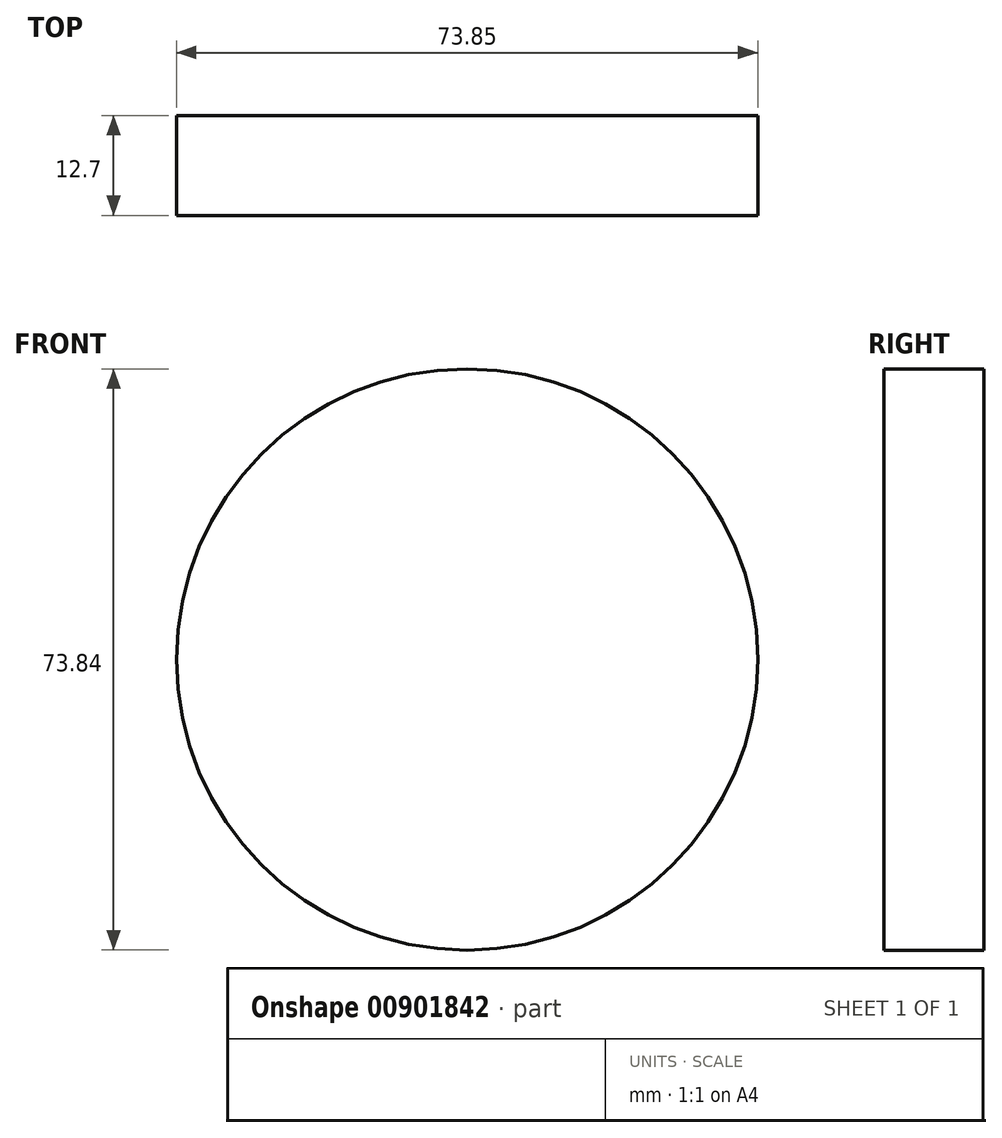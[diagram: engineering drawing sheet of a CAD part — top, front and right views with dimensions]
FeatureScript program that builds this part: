
annotation { "Feature Type Name" : "Feature", "Feature Type Description" : "" }
export const myFeature = defineFeature(function(context is Context, id is Id, definition is map)
    precondition{}
    {
        {
            var Q0;
            Q0=qCreatedBy(makeId("Front.planeOp"),FACE);
            var sketch = newSketch(context, id + "F0", { "sketchPlane" : qUnion([Q0])});
            skCircle(sketch, "E0", {"center": v(-62.64, 35.2) * mm, "radius": 36.92 * mm});
            skSolve(sketch);
        }
        {
            var Q0;
            Q0=makeQuery(id+"F0.imprint","IMPRINT",FACE,{"disambiguationData":[TD([[makeQuery(id+"F0.imprint","IMPRINT",EDGE,{"derivedFrom":sQuery(id+"F0.wireOp",EDGE,"E0")}),1.0]])]});
            extrude(context, id + "F1", {"entities" : qUnion([Q0]), "depth" : 12.7 * mm, "offsetDistance" : 25.4 * mm});
        }
    });
